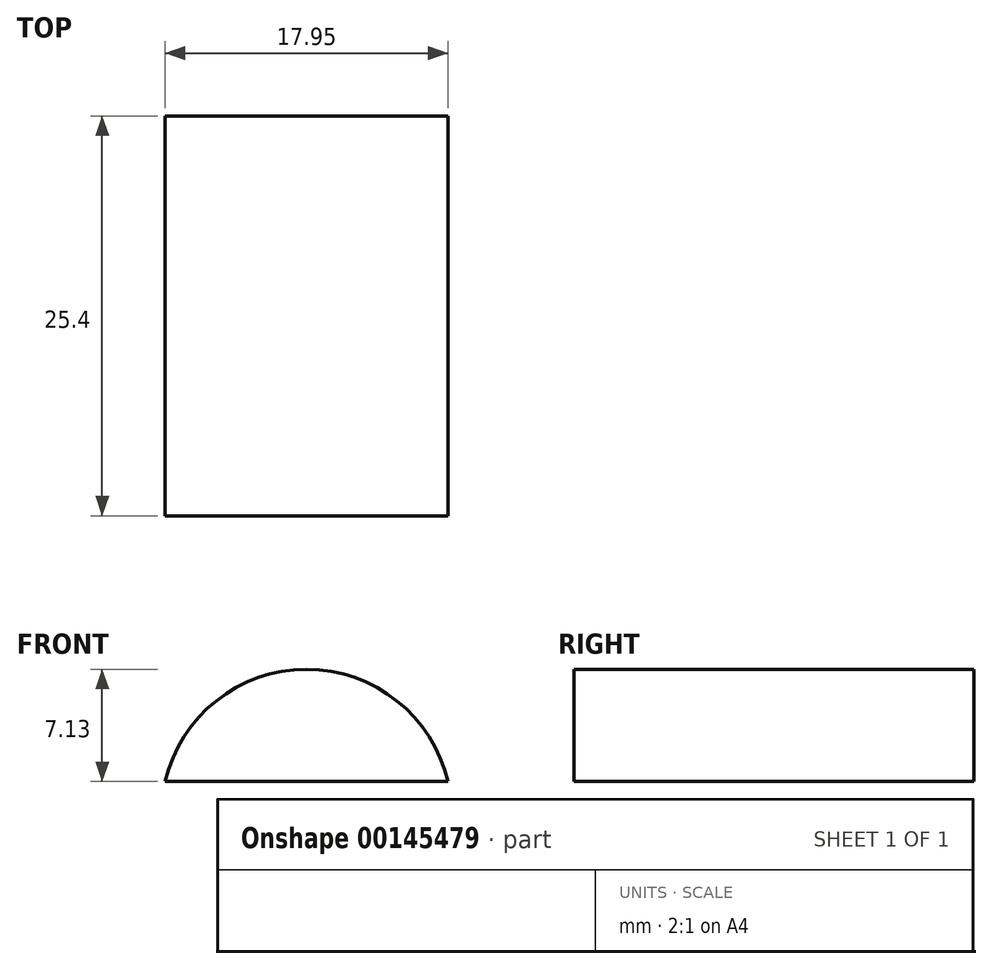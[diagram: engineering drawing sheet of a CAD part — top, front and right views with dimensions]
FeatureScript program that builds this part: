
annotation { "Feature Type Name" : "Feature", "Feature Type Description" : "" }
export const myFeature = defineFeature(function(context is Context, id is Id, definition is map)
    precondition{}
    {
        {
            var Q0;
            Q0=qCreatedBy(makeId("Front.planeOp"),FACE);
            var sketch = newSketch(context, id + "F0", { "sketchPlane" : qUnion([Q0])});
            skLineSegment(sketch, "E0", {"start": v(-23.77, 11.88) * mm, "end": v(-5.82, 11.88) * mm});
            skArc(sketch, "E1", {"start": v(-5.82, 11.88) * mm, "mid": v(-14.8, 19.01) * mm, "end": v(-23.77, 11.88) * mm});
            skSolve(sketch);
        }
        {
            var Q0;
            Q0=makeQuery(id+"F0.imprint","IMPRINT",FACE,{"disambiguationData":[TD([[makeQuery(id+"F0.imprint","IMPRINT",EDGE,{"derivedFrom":sQuery(id+"F0.wireOp",EDGE,"E0")}),1.0]])]});
            extrude(context, id + "F1", {"entities" : qUnion([Q0]), "depth" : 25.4 * mm});
        }
    });
